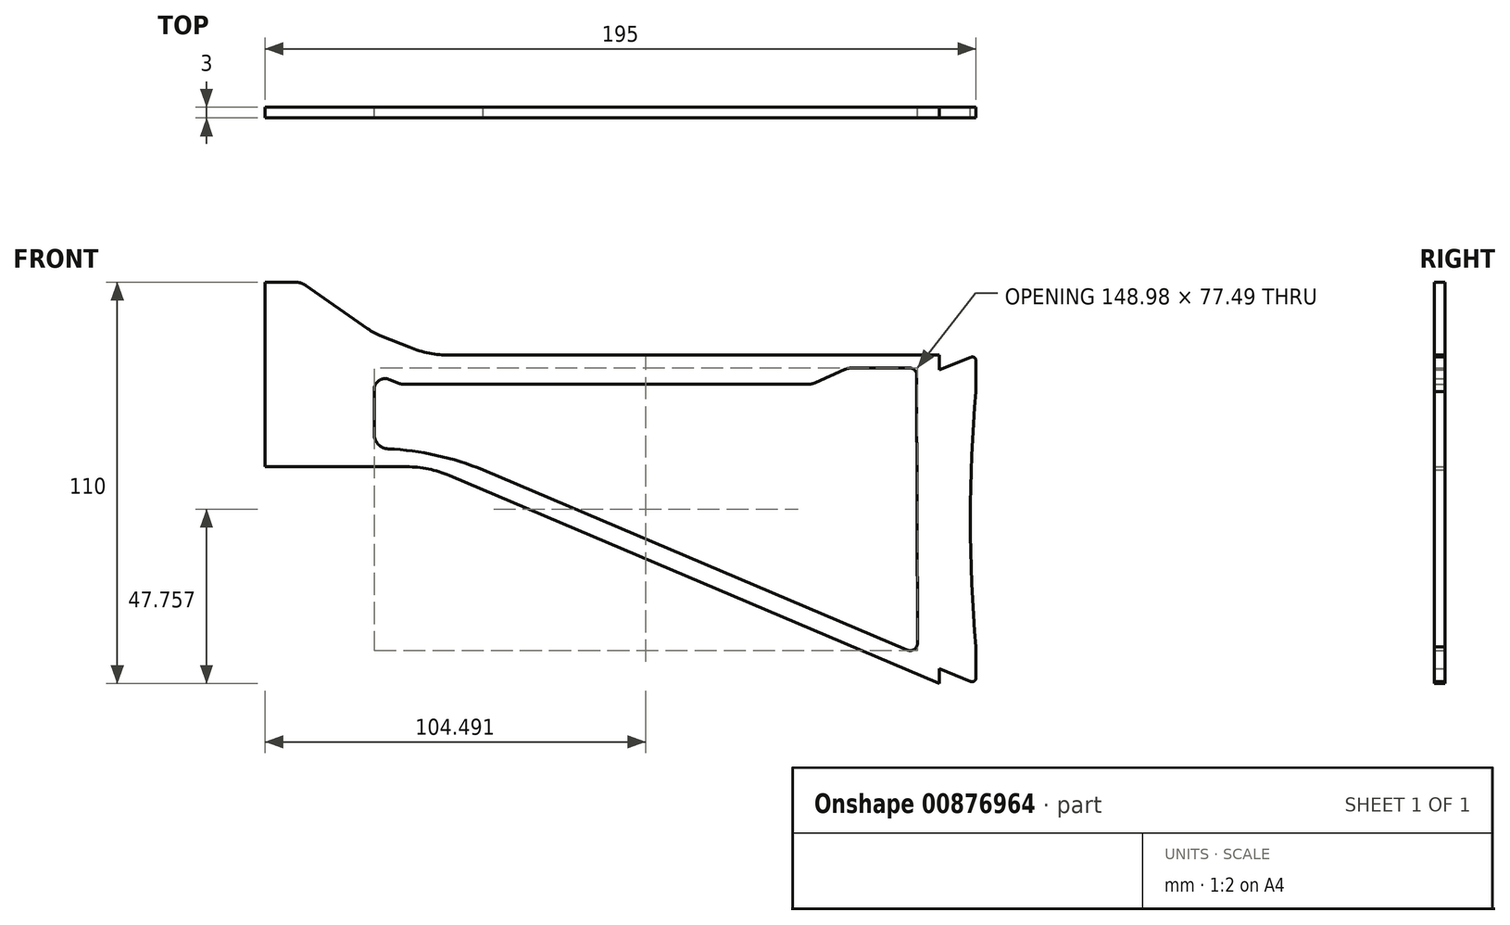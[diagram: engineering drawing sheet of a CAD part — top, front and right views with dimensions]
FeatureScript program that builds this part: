
annotation { "Feature Type Name" : "Feature", "Feature Type Description" : "" }
export const myFeature = defineFeature(function(context is Context, id is Id, definition is map)
    precondition{}
    {
        {
            var Q0;
            Q0=qCreatedBy(makeId("Front.planeOp"),FACE);
            var sketch = newSketch(context, id + "F0", { "sketchPlane" : qUnion([Q0])});
            skLineSegment(sketch, "E0", {"start": v(0, 0) * mm, "end": v(0, -50.6) * mm});
            skLineSegment(sketch, "E1", {"start": v(0, 0) * mm, "end": v(8.42, 0) * mm});
            skLineSegment(sketch, "E2", {"start": v(11.3, -0.9) * mm, "end": v(28.1, -12.68) * mm});
            skLineSegment(sketch, "E3", {"start": v(32.15, -14.86) * mm, "end": v(39.64, -17.86) * mm});
            skLineSegment(sketch, "E4", {"start": v(50.77, -20) * mm, "end": v(185, -20) * mm});
            skLineSegment(sketch, "E5", {"start": v(185, -20) * mm, "end": v(185, -24) * mm});
            skLineSegment(sketch, "E6", {"start": v(185, -24) * mm, "end": v(193.63, -20.55) * mm});
            skLineSegment(sketch, "E7", {"start": v(195, -21.48) * mm, "end": v(195, -30) * mm});
            skLineSegment(sketch, "E8", {"start": v(0, -50.6) * mm, "end": v(38.9, -50.6) * mm});
            skLineSegment(sketch, "E9", {"start": v(50.62, -53) * mm, "end": v(185, -110) * mm});
            skLineSegment(sketch, "E10", {"start": v(185, -110) * mm, "end": v(185, -106) * mm});
            skLineSegment(sketch, "E11", {"start": v(185, -106) * mm, "end": v(193.63, -109.45) * mm});
            skLineSegment(sketch, "E12", {"start": v(195, -108.52) * mm, "end": v(195, -100) * mm});
            skArc(sketch, "E13", {"start": v(195, -30) * mm, "mid": v(193.47, -65) * mm, "end": v(195, -100) * mm});
            skPoint(sketch, "E14.visualSharp", {"position": v(10, 0) * mm});
            skArc(sketch, "E14.filletArc", {"start": v(11.3, -0.9) * mm, "mid": v(9.93, -0.23) * mm, "end": v(8.42, 0) * mm});
            skPoint(sketch, "E15.visualSharp", {"position": v(30, -14) * mm});
            skArc(sketch, "E15.filletArc", {"start": v(28.1, -12.68) * mm, "mid": v(30.06, -13.89) * mm, "end": v(32.15, -14.86) * mm});
            skPoint(sketch, "E16.visualSharp", {"position": v(45, -20) * mm});
            skArc(sketch, "E16.filletArc", {"start": v(39.64, -17.86) * mm, "mid": v(45.1, -19.46) * mm, "end": v(50.77, -20) * mm});
            skPoint(sketch, "E17.visualSharp", {"position": v(45, -50.6) * mm});
            skArc(sketch, "E17.filletArc", {"start": v(50.62, -53) * mm, "mid": v(44.88, -51.21) * mm, "end": v(38.9, -50.6) * mm});
            skPoint(sketch, "E18.visualSharp", {"position": v(195, -20) * mm});
            skArc(sketch, "E18.filletArc", {"start": v(195, -21.48) * mm, "mid": v(194.56, -20.65) * mm, "end": v(193.63, -20.55) * mm});
            skPoint(sketch, "E19.visualSharp", {"position": v(195, -110) * mm});
            skArc(sketch, "E19.filletArc", {"start": v(193.63, -109.45) * mm, "mid": v(194.56, -109.35) * mm, "end": v(195, -108.52) * mm});
            skPoint(sketch, "E20.visualSharp", {"position": v(59.85, -51.48) * mm});
            skPoint(sketch, "E21", {"position": v(30, -45.6) * mm});
            skArc(sketch, "E22", {"start": v(33.81, -45.7) * mm, "mid": v(47.08, -47.47) * mm, "end": v(59.85, -51.48) * mm});
            skLineSegment(sketch, "E23", {"start": v(30, -41.7) * mm, "end": v(30, -29.43) * mm});
            skPoint(sketch, "E24", {"position": v(37.5, -28) * mm});
            skLineSegment(sketch, "E25", {"start": v(34.11, -26.64) * mm, "end": v(36.97, -27.79) * mm});
            skPoint(sketch, "E26", {"position": v(150, -28) * mm});
            skLineSegment(sketch, "E27", {"start": v(150.98, -27.56) * mm, "end": v(159.02, -23.94) * mm});
            skLineSegment(sketch, "E28", {"start": v(148.93, -28) * mm, "end": v(38.08, -28) * mm});
            skPoint(sketch, "E29.visualSharp", {"position": v(160, -23.5) * mm});
            skArc(sketch, "E29.filletArc", {"start": v(161.07, -23.5) * mm, "mid": v(160.02, -23.61) * mm, "end": v(159.02, -23.94) * mm});
            skArc(sketch, "E30.filletArc", {"start": v(148.93, -28) * mm, "mid": v(149.98, -27.89) * mm, "end": v(150.98, -27.56) * mm});
            skArc(sketch, "E31.filletArc", {"start": v(30, -41.7) * mm, "mid": v(31.1, -44.46) * mm, "end": v(33.81, -45.7) * mm});
            skPoint(sketch, "E32.visualSharp", {"position": v(30, -25) * mm});
            skArc(sketch, "E32.filletArc", {"start": v(34.11, -26.64) * mm, "mid": v(31.32, -26.95) * mm, "end": v(30, -29.43) * mm});
            skArc(sketch, "E33.filletArc", {"start": v(36.97, -27.79) * mm, "mid": v(37.52, -27.95) * mm, "end": v(38.08, -28) * mm});
            skPoint(sketch, "E34", {"position": v(178.78, -23.5) * mm});
            skLineSegment(sketch, "E35", {"start": v(178.98, -98.99) * mm, "end": v(178.78, -25.5) * mm});
            skLineSegment(sketch, "E36", {"start": v(161.07, -23.5) * mm, "end": v(176.78, -23.5) * mm});
            skLineSegment(sketch, "E37", {"start": v(59.85, -51.48) * mm, "end": v(176.2, -100.84) * mm});
            skPoint(sketch, "E38.visualSharp", {"position": v(179, -102.02) * mm});
            skArc(sketch, "E38.filletArc", {"start": v(176.2, -100.84) * mm, "mid": v(178.09, -100.66) * mm, "end": v(178.98, -98.99) * mm});
            skArc(sketch, "E39.filletArc", {"start": v(178.78, -25.5) * mm, "mid": v(178.2, -24.08) * mm, "end": v(176.78, -23.5) * mm});
            skSolve(sketch);
        }
        {
            var Q0;
            Q0=makeQuery(id+"F0.imprint","IMPRINT",FACE,{"disambiguationData":[TD([[makeQuery(id+"F0.imprint","IMPRINT",EDGE,{"derivedFrom":sQuery(id+"F0.wireOp",EDGE,"E0")}),1.0]])]});
            extrude(context, id + "F1", {"entities" : qUnion([Q0]), "depth" : 3 * mm, "offsetDistance" : 25 * mm});
        }
    });
